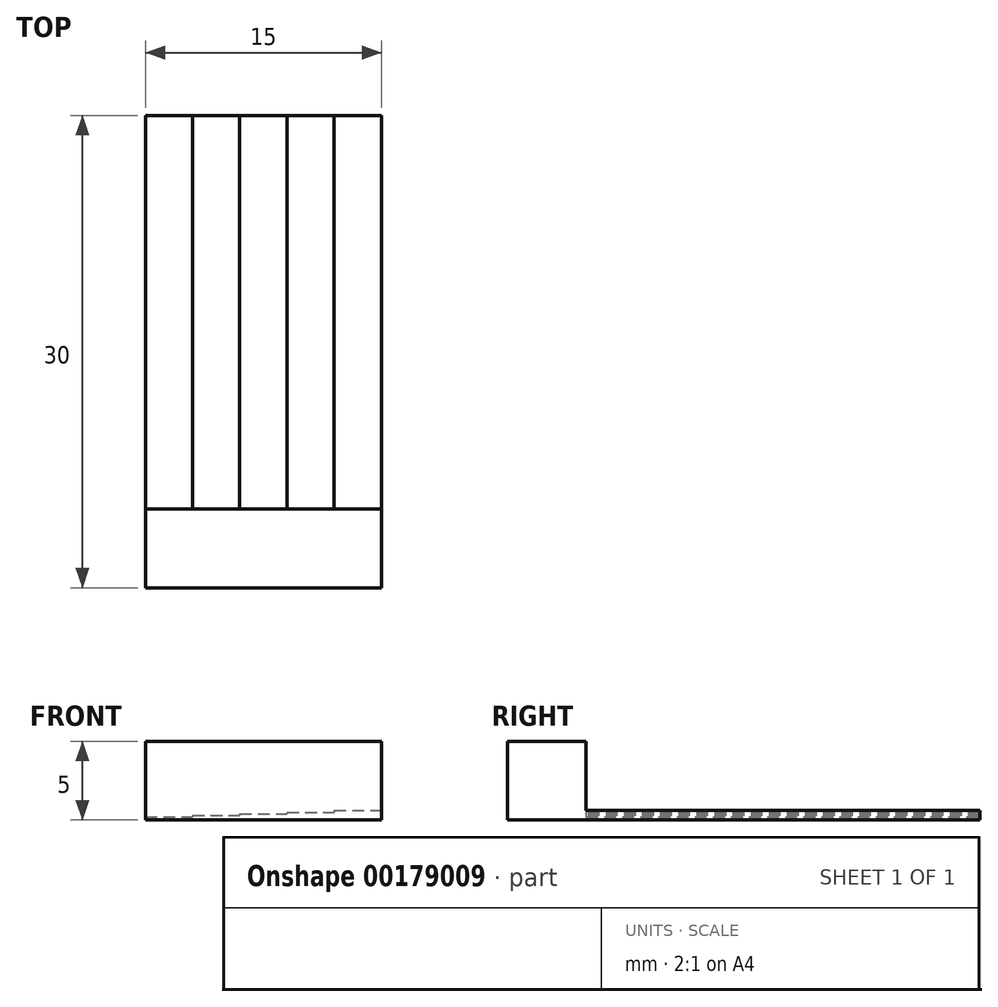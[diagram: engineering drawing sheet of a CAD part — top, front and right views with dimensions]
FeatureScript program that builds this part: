
annotation { "Feature Type Name" : "Feature", "Feature Type Description" : "" }
export const myFeature = defineFeature(function(context is Context, id is Id, definition is map)
    precondition{}
    {
        {
            var Q0;
            Q0=qCreatedBy(makeId("Top.planeOp"),FACE);
            var sketch = newSketch(context, id + "F0", { "sketchPlane" : qUnion([Q0])});
            skLineSegment(sketch, "E0.bottom", {"start": v(7.5, -15) * mm, "end": v(-7.5, -15) * mm});
            skLineSegment(sketch, "E0.top", {"start": v(7.5, 15) * mm, "end": v(-7.5, 15) * mm});
            skLineSegment(sketch, "E0.left", {"start": v(7.5, -15) * mm, "end": v(7.5, 15) * mm});
            skLineSegment(sketch, "E0.right", {"start": v(-7.5, -15) * mm, "end": v(-7.5, 15) * mm});
            skPoint(sketch, "E0.middle", {"position": v(0, 0) * mm});
            skLineSegment(sketch, "E1", {"start": v(-7.5, -10) * mm, "end": v(7.5, -10) * mm});
            skLineSegment(sketch, "E2", {"start": v(-4.5, 15) * mm, "end": v(-4.5, -10) * mm});
            skLineSegment(sketch, "E3.1.0.0", {"start": v(-1.5, 15) * mm, "end": v(-1.5, -10) * mm});
            skLineSegment(sketch, "E3.2.0.0", {"start": v(1.5, 15) * mm, "end": v(1.5, -10) * mm});
            skLineSegment(sketch, "E3.3.0.0", {"start": v(4.5, 15) * mm, "end": v(4.5, -10) * mm});
            skLineSegment(sketch, "E3.direction1", {"start": v(-4.5, -10) * mm, "end": v(-1.5, -10) * mm, "construction": true});
            skSolve(sketch);
        }
        {
            var Q0;
            {var subQ4=sQuery(id+"F0.wireOp",EDGE,"E0.bottom");Q0=makeQuery(id+"F0.imprint","IMPRINT",FACE,{"disambiguationData":[TD([[makeQuery(id+"F0.imprint","IMPRINT",EDGE,{"derivedFrom":subQ4}),-1.0]])]});}
            extrude(context, id + "F1", {"entities" : qUnion([Q0]), "depth" : 5 * mm});
        }
        {
            var Q0;
            {var subQ3=sQuery(id+"F0.wireOp",EDGE,"E2");Q0=makeQuery(id+"F0.imprint","IMPRINT",FACE,{"disambiguationData":[TD([[makeQuery(id+"F0.imprint","IMPRINT",EDGE,{"derivedFrom":subQ3}),-1.0]])]});}
            extrude(context, id + "F2", {"entities" : qUnion([Q0]), "operationType" : NewBodyOperationType.ADD, "depth" : 0.2 * mm});
        }
        {
            var Q0;
            {var subQ0=sQuery(id+"F0.wireOp",EDGE,"E2");Q0=makeQuery(id+"F0.imprint","IMPRINT",FACE,{"disambiguationData":[TD([[makeQuery(id+"F0.imprint","IMPRINT",EDGE,{"derivedFrom":subQ0}),1.0]])]});}
            extrude(context, id + "F3", {"entities" : qUnion([Q0]), "operationType" : NewBodyOperationType.ADD, "depth" : 0.3 * mm});
        }
        {
            var Q0;
            {var subQ0=sQuery(id+"F0.wireOp",EDGE,"E3.1.0.0");Q0=makeQuery(id+"F0.imprint","IMPRINT",FACE,{"disambiguationData":[TD([[makeQuery(id+"F0.imprint","IMPRINT",EDGE,{"derivedFrom":subQ0}),1.0]])]});}
            extrude(context, id + "F4", {"entities" : qUnion([Q0]), "operationType" : NewBodyOperationType.ADD, "depth" : 0.4 * mm});
        }
        {
            var Q0;
            {var subQ0=sQuery(id+"F0.wireOp",EDGE,"E3.2.0.0");Q0=makeQuery(id+"F0.imprint","IMPRINT",FACE,{"disambiguationData":[TD([[makeQuery(id+"F0.imprint","IMPRINT",EDGE,{"derivedFrom":subQ0}),1.0]])]});}
            extrude(context, id + "F5", {"entities" : qUnion([Q0]), "operationType" : NewBodyOperationType.ADD, "depth" : 0.5 * mm});
        }
        {
            var Q0;
            {var subQ3=sQuery(id+"F0.wireOp",EDGE,"E3.3.0.0");Q0=makeQuery(id+"F0.imprint","IMPRINT",FACE,{"disambiguationData":[TD([[makeQuery(id+"F0.imprint","IMPRINT",EDGE,{"derivedFrom":subQ3}),1.0]])]});}
            extrude(context, id + "F6", {"entities" : qUnion([Q0]), "operationType" : NewBodyOperationType.ADD, "depth" : 0.6 * mm});
        }
    });
